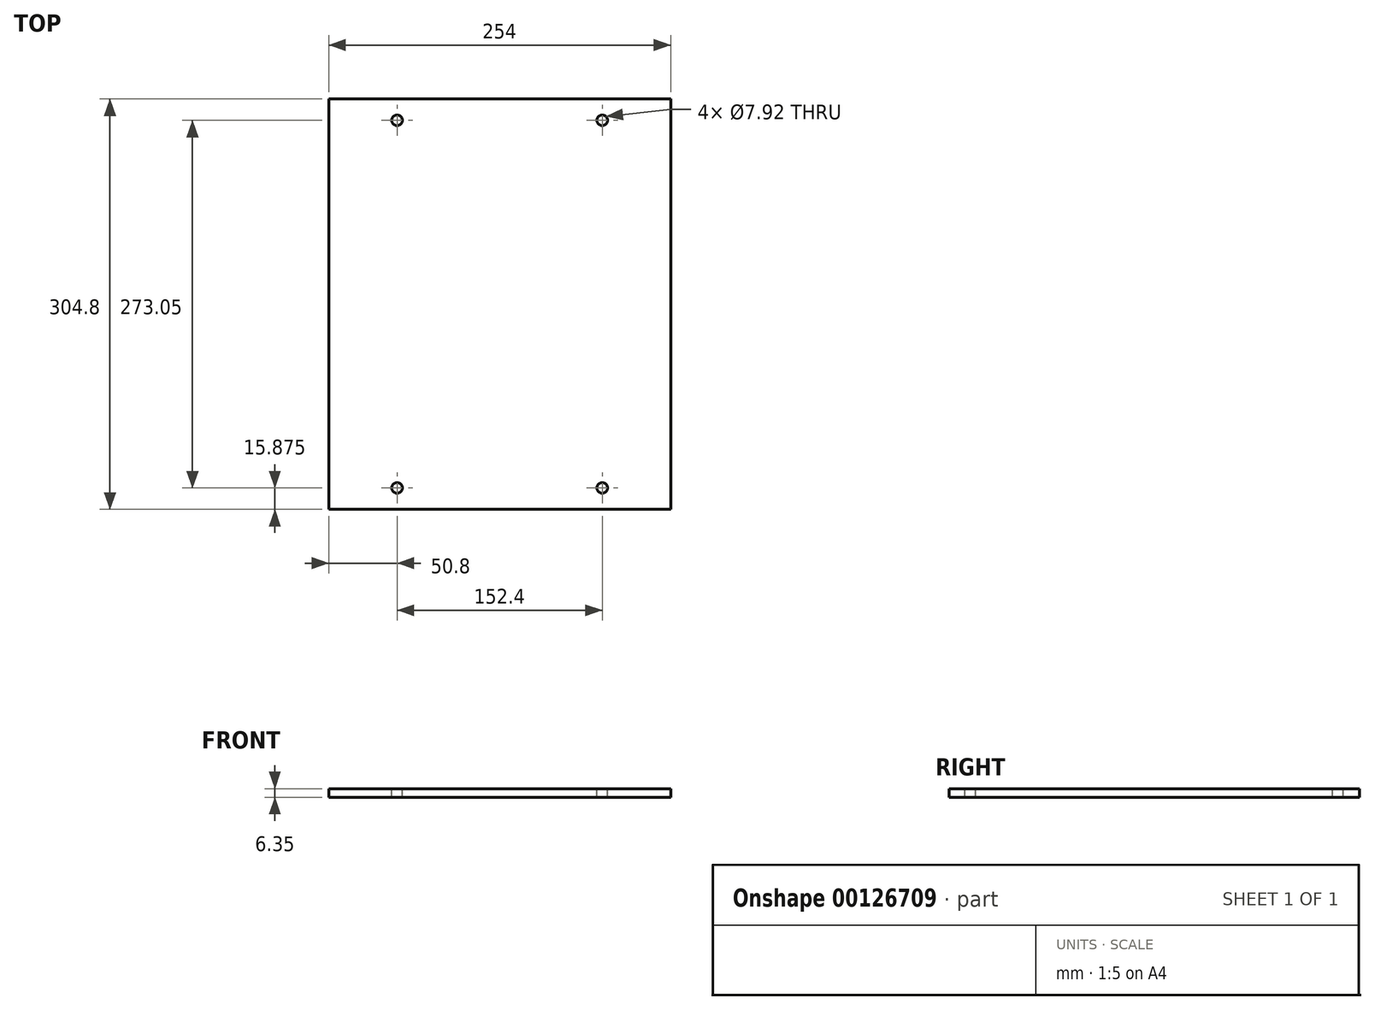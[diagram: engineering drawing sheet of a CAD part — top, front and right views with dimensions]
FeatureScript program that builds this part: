
annotation { "Feature Type Name" : "Feature", "Feature Type Description" : "" }
export const myFeature = defineFeature(function(context is Context, id is Id, definition is map)
    precondition{}
    {
        {
            var Q0;
            Q0=qCreatedBy(makeId("Top.planeOp"),FACE);
            var sketch = newSketch(context, id + "F0", { "sketchPlane" : qUnion([Q0])});
            skLineSegment(sketch, "E0.bottom", {"start": v(0, 0) * mm, "end": v(254, 0) * mm});
            skLineSegment(sketch, "E0.top", {"start": v(0, 304.8) * mm, "end": v(254, 304.8) * mm});
            skLineSegment(sketch, "E0.left", {"start": v(0, 0) * mm, "end": v(0, 304.8) * mm});
            skLineSegment(sketch, "E0.right", {"start": v(254, 0) * mm, "end": v(254, 304.8) * mm});
            skSolve(sketch);
        }
        {
            var Q0;
            Q0 = qSketchRegion(id + "F0", true);
            extrude(context, id + "F1", {"entities" : qUnion([Q0]), "oppositeDirection" : true, "depth" : 6.35 * mm});
        }
        {
            var Q0;
            Q0=makeQuery(id+"F1.opExtrude","CAP_FACE",FACE,{"disambiguationData":[OSD([sQuery(id+"F0.wireOp",EDGE,"E0.bottom"),sQuery(id+"F0.wireOp",EDGE,"E0.top"),sQuery(id+"F0.wireOp",EDGE,"E0.left"),sQuery(id+"F0.wireOp",EDGE,"E0.right")])],"isStart":true});
            var sketch = newSketch(context, id + "F2", { "sketchPlane" : qUnion([Q0])});
            skCircle(sketch, "E1", {"center": v(50.8, 288.93) * mm, "radius": 3.96 * mm});
            skCircle(sketch, "E2", {"center": v(203.2, 288.93) * mm, "radius": 3.96 * mm});
            skCircle(sketch, "E3", {"center": v(203.2, 15.88) * mm, "radius": 3.96 * mm});
            skCircle(sketch, "E4", {"center": v(50.8, 15.88) * mm, "radius": 3.96 * mm});
            skSolve(sketch);
        }
        {
            var Q0;
            Q0=sQuery(id+"F2.wireOp",VERTEX,"E1.center");
            var Q1;
            Q1=makeQuery(id+"F1.opExtrude","SWEPT_BODY",BODY,{"disambiguationData":[OSD([sQuery(id+"F0.wireOp",EDGE,"E0.bottom"),sQuery(id+"F0.wireOp",EDGE,"E0.top"),sQuery(id+"F0.wireOp",EDGE,"E0.left"),sQuery(id+"F0.wireOp",EDGE,"E0.right")])]});
            hole(context, id + "F3", {"style" : HoleStyle.SIMPLE, "endStyle" : HoleEndStyle.THROUGH, "holeDiameter" : 7.92 * mm, "locations" : qUnion([Q0]), "scope" : qUnion([Q1]), "isTappedThrough" : true});
        }
        {
            var Q0;
            Q0=sQuery(id+"F2.wireOp",VERTEX,"E2.center");
            var Q1;
            Q1=makeQuery(id+"F1.opExtrude","SWEPT_BODY",BODY,{"disambiguationData":[OSD([sQuery(id+"F0.wireOp",EDGE,"E0.bottom"),sQuery(id+"F0.wireOp",EDGE,"E0.top"),sQuery(id+"F0.wireOp",EDGE,"E0.left"),sQuery(id+"F0.wireOp",EDGE,"E0.right")])]});
            hole(context, id + "F4", {"style" : HoleStyle.SIMPLE, "endStyle" : HoleEndStyle.THROUGH, "holeDiameter" : 7.92 * mm, "locations" : qUnion([Q0]), "scope" : qUnion([Q1]), "isTappedThrough" : true});
        }
        {
            var Q0;
            Q0=sQuery(id+"F2.wireOp",VERTEX,"E3.center");
            var Q1;
            Q1=makeQuery(id+"F1.opExtrude","SWEPT_BODY",BODY,{"disambiguationData":[OSD([sQuery(id+"F0.wireOp",EDGE,"E0.bottom"),sQuery(id+"F0.wireOp",EDGE,"E0.top"),sQuery(id+"F0.wireOp",EDGE,"E0.left"),sQuery(id+"F0.wireOp",EDGE,"E0.right")])]});
            hole(context, id + "F5", {"style" : HoleStyle.SIMPLE, "endStyle" : HoleEndStyle.THROUGH, "holeDiameter" : 7.92 * mm, "locations" : qUnion([Q0]), "scope" : qUnion([Q1]), "isTappedThrough" : true});
        }
        {
            var Q0;
            Q0=sQuery(id+"F2.wireOp",VERTEX,"E4.center");
            var Q1;
            Q1=makeQuery(id+"F1.opExtrude","SWEPT_BODY",BODY,{"disambiguationData":[OSD([sQuery(id+"F0.wireOp",EDGE,"E0.bottom"),sQuery(id+"F0.wireOp",EDGE,"E0.top"),sQuery(id+"F0.wireOp",EDGE,"E0.left"),sQuery(id+"F0.wireOp",EDGE,"E0.right")])]});
            hole(context, id + "F6", {"style" : HoleStyle.SIMPLE, "endStyle" : HoleEndStyle.THROUGH, "holeDiameter" : 7.92 * mm, "locations" : qUnion([Q0]), "scope" : qUnion([Q1]), "isTappedThrough" : true});
        }
    });
